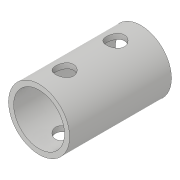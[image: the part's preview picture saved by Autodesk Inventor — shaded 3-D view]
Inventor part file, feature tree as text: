
AUTODESK INVENTOR PART (.ipt)
format: ipt  version: 2019 (Build 230136000, 136)  size: 115,712 bytes
history: native  units: mm
features: sketch x5, extrude x3
ambient origin geometry x8: Origin, YZ Plane, XZ Plane, XY Plane, X Axis, Y Axis, Z Axis, Center Point
bodies: Solid1 (feature_tree)
feature tree (8):
  sketch  "Sketch1"  dims[d0=12.0mm d1=20.0mm d2=0.0mm]
  extrude  "Extrusion1"  Depth=20.0mm TaperAngle=0.0deg
  sketch  "Sketch3"  dims[d6=5.0mm d7=10.0mm]
  extrude  "Extrusion2"  Depth=10.0mm TaperAngle=0.0deg
  extrude  "Extrusion3"  Depth=10.0mm
  sketch  "Sketch2"  dims[d3=10.0mm d4=20.0mm d5=0.0mm]
  sketch  "Sketch4"  dims[d8=3.5mm]
  sketch  "Sketch5"  dims[d9=3.5mm d10=0.0mm d11=0.0mm]
